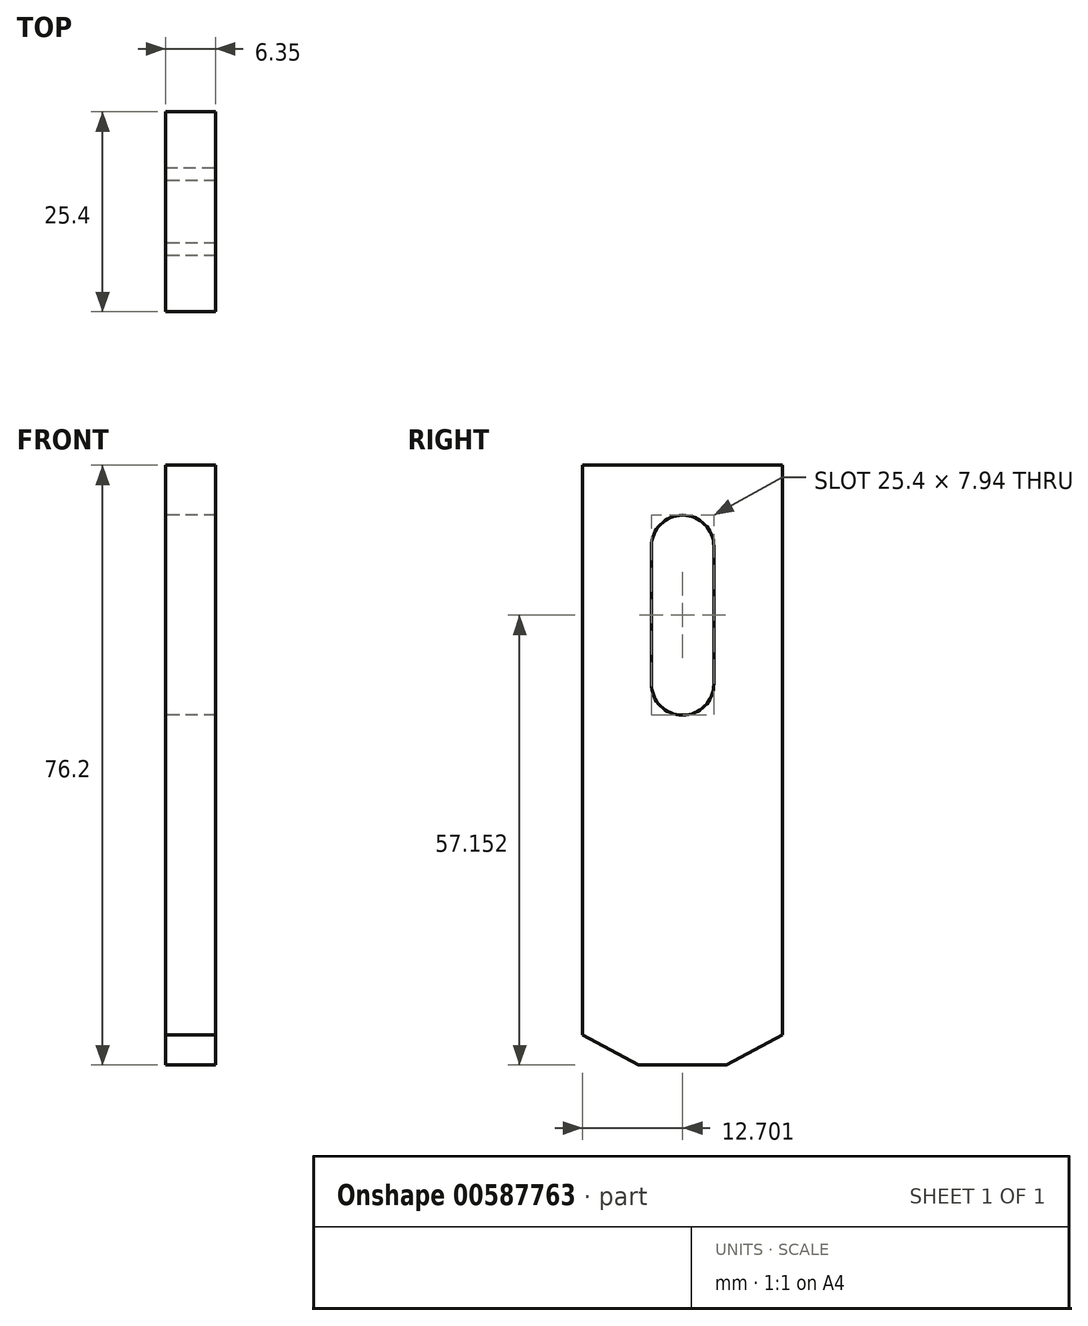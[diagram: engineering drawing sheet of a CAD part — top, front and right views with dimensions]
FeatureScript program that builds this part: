
annotation { "Feature Type Name" : "Feature", "Feature Type Description" : "" }
export const myFeature = defineFeature(function(context is Context, id is Id, definition is map)
    precondition{}
    {
        {
            var Q0;
            Q0=qCreatedBy(makeId("Right.planeOp"),FACE);
            var sketch = newSketch(context, id + "F0", { "sketchPlane" : qUnion([Q0])});
            skLineSegment(sketch, "E0.bottom", {"start": v(1.4, 26.11) * mm, "end": v(26.8, 26.11) * mm});
            skLineSegment(sketch, "E0.top", {"start": v(1.4, -50.09) * mm, "end": v(26.8, -50.09) * mm});
            skLineSegment(sketch, "E0.left", {"start": v(1.4, 26.11) * mm, "end": v(1.4, -50.09) * mm});
            skLineSegment(sketch, "E0.right", {"start": v(26.8, 26.11) * mm, "end": v(26.8, -50.09) * mm});
            skLineSegment(sketch, "E1", {"start": v(26.8, 9.88) * mm, "end": v(26.8, 3.79) * mm});
            skArc(sketch, "E2", {"start": v(18.06, 15.8) * mm, "mid": v(14.1, 19.76) * mm, "end": v(10.12, 15.8) * mm});
            skArc(sketch, "E3", {"start": v(10.12, -1.67) * mm, "mid": v(14.1, -5.64) * mm, "end": v(18.06, -1.67) * mm});
            skLineSegment(sketch, "E4", {"start": v(18.06, 15.8) * mm, "end": v(18.06, -1.67) * mm});
            skLineSegment(sketch, "E5", {"start": v(10.12, 15.8) * mm, "end": v(10.12, -1.67) * mm});
            skSolve(sketch);
        }
        {
            var Q0;
            {var subQ1=sQuery(id+"F0.wireOp",EDGE,"E0.bottom");Q0=makeQuery(id+"F0.imprint","IMPRINT",FACE,{"disambiguationData":[TD([[makeQuery(id+"F0.imprint","IMPRINT",EDGE,{"derivedFrom":subQ1}),-1.0]])]});}
            extrude(context, id + "F1", {"entities" : qUnion([Q0]), "depth" : 6.35 * mm, "offsetDistance" : 25.4 * mm});
        }
        {
            var Q0;
            Q0=makeQuery(id+"F1.opExtrude","SWEPT_EDGE",EDGE,{"disambiguationData":[OSD([sQuery(id+"F0.wireOp",EDGE,"E0.top"),sQuery(id+"F0.wireOp",EDGE,"E0.left")])]});
            var Q1;
            Q1=makeQuery(id+"F1.opExtrude","SWEPT_EDGE",EDGE,{"disambiguationData":[OSD([sQuery(id+"F0.wireOp",EDGE,"E0.top"),sQuery(id+"F0.wireOp",EDGE,"E0.right")])]});
            chamfer(context, id + "F2", {"entities" : qUnion([Q0, Q1]), "chamferType" : ChamferType.TWO_OFFSETS, "width1" : 7.11 * mm, "oppositeDirection" : false, "width2" : 3.8 * mm, "tangentPropagation" : true});
        }
    });
